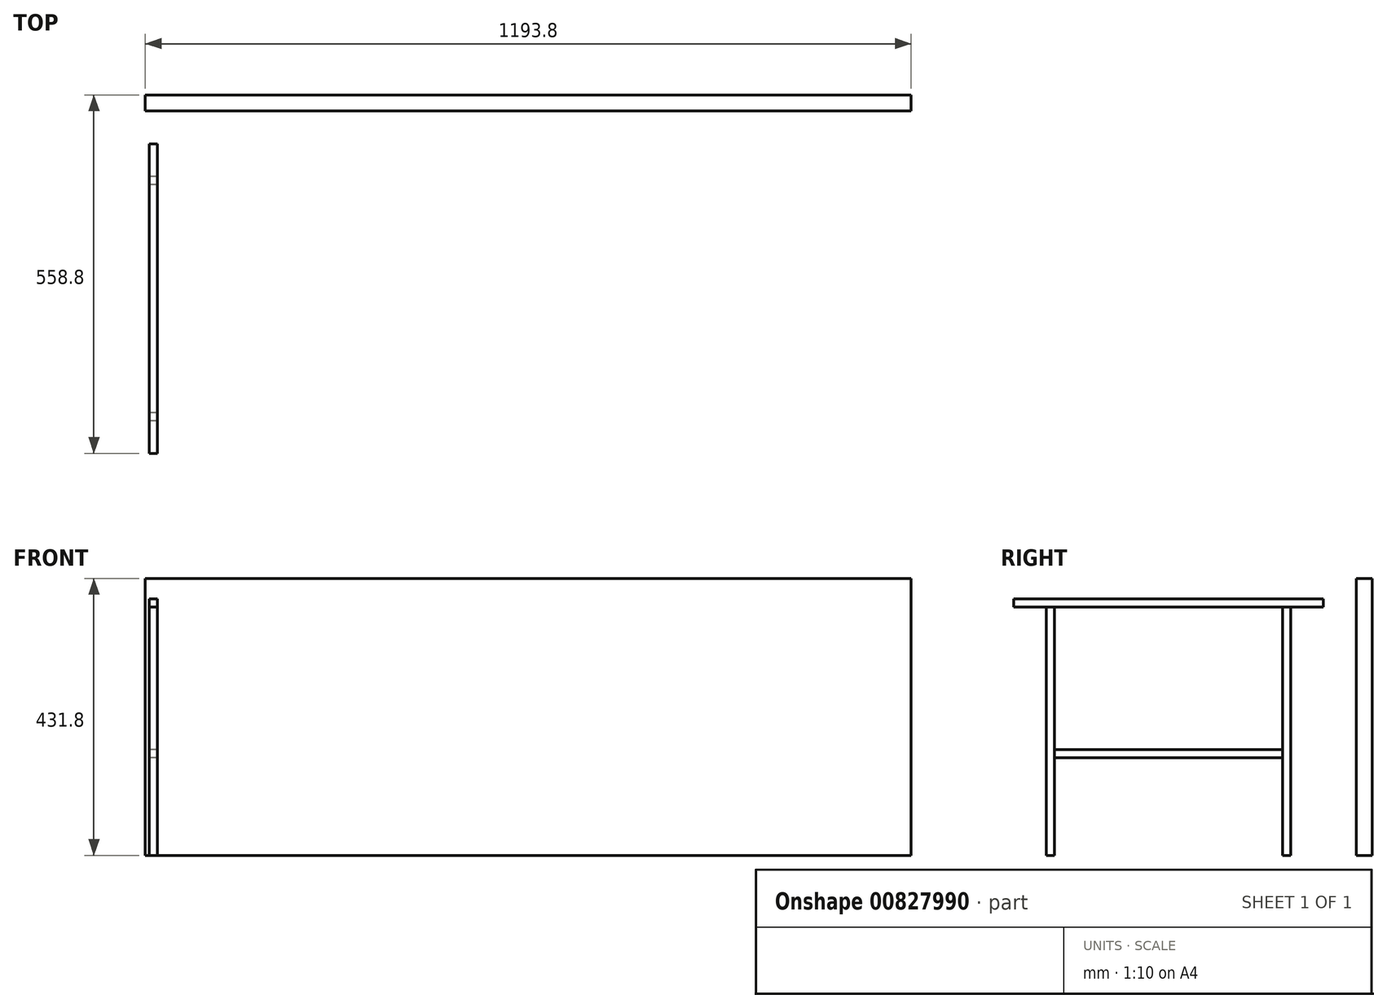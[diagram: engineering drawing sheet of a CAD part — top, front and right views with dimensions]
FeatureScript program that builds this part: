
annotation { "Feature Type Name" : "Feature", "Feature Type Description" : "" }
export const myFeature = defineFeature(function(context is Context, id is Id, definition is map)
    precondition{}
    {
        {
            assignVariable(context, id + "F0", {"name" : "Depth", "anyValue" : 25});
        }
        {
            assignVariable(context, id + "F1", {"name" : "EndInset", "anyValue" : 6});
        }
        {
            var Q0;
            Q0=qCreatedBy(makeId("Front.planeOp"),FACE);
            var sketch = newSketch(context, id + "F2", { "sketchPlane" : qUnion([Q0])});
            skLineSegment(sketch, "E0.bottom", {"start": v(0, 0) * mm, "end": v(1193.8, 0) * mm});
            skLineSegment(sketch, "E0.top", {"start": v(0, 431.8) * mm, "end": v(1193.8, 431.8) * mm});
            skLineSegment(sketch, "E0.left", {"start": v(0, 0) * mm, "end": v(0, 431.8) * mm});
            skLineSegment(sketch, "E0.right", {"start": v(1193.8, 0) * mm, "end": v(1193.8, 431.8) * mm});
            skSolve(sketch);
        }
        {
            var Q0;
            Q0=makeQuery(id+"F2.imprint","IMPRINT",FACE,{"disambiguationData":[TD([[makeQuery(id+"F2.imprint","IMPRINT",EDGE,{"derivedFrom":sQuery(id+"F2.wireOp",EDGE,"E0.bottom")}),1.0]])]});
            var Q1;
            Q1=sQuery(id+"F2.wireOp",EDGE,"E0.top");
            var Q2;
            Q2=sQuery(id+"F2.wireOp",EDGE,"E0.left");
            var Q3;
            Q3=sQuery(id+"F2.wireOp",EDGE,"E0.bottom");
            var Q4;
            Q4=sQuery(id+"F2.wireOp",EDGE,"E0.right");
            extrude(context, id + "F3", {"entities" : qUnion([Q0]), "surfaceEntities" : qUnion([Q1, Q2, Q3, Q4]), "depth" : (getVariable(context, 'Depth')) * mm, "offsetDistance" : 25.4 * mm});
        }
        {
            var Q0;
            Q0=makeQuery(id+"F3.opExtrude","SWEPT_FACE",FACE,{"disambiguationData":[OSD([sQuery(id+"F2.wireOp",EDGE,"E0.left")])]});
            cPlane(context, id + "F4", {"entities" : qUnion([Q0]), "cplaneType" : CPlaneType.OFFSET, "offset" : (getVariable(context, 'EndInset')) * mm, "oppositeDirection" : true, "width" : 152.4 * mm, "height" : 152.4 * mm});
        }
        {
            var Q0;
            Q0=qCreatedBy(id+"F4.planeOp",FACE);
            var sketch = newSketch(context, id + "F5", { "sketchPlane" : qUnion([Q0])});
            skLineSegment(sketch, "E1.bottom", {"start": v(127, 0) * mm, "end": v(139.7, 0) * mm});
            skLineSegment(sketch, "E1.top", {"start": v(127, 387.35) * mm, "end": v(139.7, 387.35) * mm});
            skLineSegment(sketch, "E1.left", {"start": v(127, 0) * mm, "end": v(127, 387.35) * mm});
            skLineSegment(sketch, "E1.right", {"start": v(139.7, 0) * mm, "end": v(139.7, 387.35) * mm});
            skLineSegment(sketch, "E2.bottom", {"start": v(76.2, 400.05) * mm, "end": v(558.8, 400.05) * mm});
            skLineSegment(sketch, "E2.top", {"start": v(76.2, 387.35) * mm, "end": v(558.8, 387.35) * mm});
            skLineSegment(sketch, "E2.left", {"start": v(76.2, 400.05) * mm, "end": v(76.2, 387.35) * mm});
            skLineSegment(sketch, "E2.right", {"start": v(558.8, 400.05) * mm, "end": v(558.8, 387.35) * mm});
            skLineSegment(sketch, "E3.bottom", {"start": v(495.3, 387.35) * mm, "end": v(508, 387.35) * mm});
            skLineSegment(sketch, "E3.top", {"start": v(495.3, 0) * mm, "end": v(508, 0) * mm});
            skLineSegment(sketch, "E3.left", {"start": v(495.3, 387.35) * mm, "end": v(495.3, 0) * mm});
            skLineSegment(sketch, "E3.right", {"start": v(508, 387.35) * mm, "end": v(508, 0) * mm});
            skLineSegment(sketch, "E4", {"start": v(317.5, 431.8) * mm, "end": v(317.5, 400.05) * mm, "construction": true});
            skLineSegment(sketch, "E5", {"start": v(317.5, 400.05) * mm, "end": v(317.5, 0) * mm, "construction": true});
            skLineSegment(sketch, "E6.bottom", {"start": v(139.7, 165.1) * mm, "end": v(495.3, 165.1) * mm});
            skLineSegment(sketch, "E6.top", {"start": v(139.7, 152.4) * mm, "end": v(495.3, 152.4) * mm});
            skLineSegment(sketch, "E6.left", {"start": v(139.7, 165.1) * mm, "end": v(139.7, 152.4) * mm});
            skLineSegment(sketch, "E6.right", {"start": v(495.3, 165.1) * mm, "end": v(495.3, 152.4) * mm});
            skSolve(sketch);
        }
        {
            var Q0;
            {var subQ1=sQuery(id+"F5.wireOp",EDGE,"E1.top");Q0=makeQuery(id+"F5.imprint","IMPRINT",FACE,{"disambiguationData":[TD([[makeQuery(id+"F5.imprint","IMPRINT",EDGE,{"derivedFrom":subQ1}),1.0]])]});}
            extrude(context, id + "F6", {"entities" : qUnion([Q0]), "oppositeDirection" : true, "depth" : 12.7 * mm, "offsetDistance" : 25.4 * mm});
        }
        {
            var Q0;
            {var subQ3=sQuery(id+"F5.wireOp",EDGE,"E1.bottom");Q0=makeQuery(id+"F5.imprint","IMPRINT",FACE,{"disambiguationData":[TD([[makeQuery(id+"F5.imprint","IMPRINT",EDGE,{"derivedFrom":subQ3}),1.0]])]});}
            extrude(context, id + "F7", {"entities" : qUnion([Q0]), "oppositeDirection" : true, "depth" : 12.7 * mm, "offsetDistance" : 25.4 * mm});
        }
        {
            var Q0;
            {var subQ0=sQuery(id+"F5.wireOp",EDGE,"E6.bottom");Q0=makeQuery(id+"F5.imprint","IMPRINT",FACE,{"disambiguationData":[TD([[makeQuery(id+"F5.imprint","IMPRINT",EDGE,{"derivedFrom":subQ0}),-1.0]])]});}
            extrude(context, id + "F8", {"entities" : qUnion([Q0]), "oppositeDirection" : true, "depth" : 12.7 * mm, "offsetDistance" : 25.4 * mm});
        }
        {
            var Q0;
            {var subQ4=sQuery(id+"F5.wireOp",EDGE,"E3.top");Q0=makeQuery(id+"F5.imprint","IMPRINT",FACE,{"disambiguationData":[TD([[makeQuery(id+"F5.imprint","IMPRINT",EDGE,{"derivedFrom":subQ4}),1.0]])]});}
            extrude(context, id + "F9", {"entities" : qUnion([Q0]), "oppositeDirection" : true, "depth" : 12.7 * mm, "offsetDistance" : 25.4 * mm});
        }
    });
